# Revit family: 712-0620-001-DN40-300
name_source: partatom
category: Pipe Accessories
units: mm (PartAtom-declared; Revit-internal decimal feet)

## family parameters
Always vertical = Yes
Cut with Voids When Loaded = No
Part Type = Breaks Into
Round Connector Dimension = Use Diameter
Shared = No
Work Plane-Based = No

## types (13) — shared parameters
DN040_PN10/16 = 712-0040-06-201
DN050_PN10/16 = 712-0050-06-201
DN065_PN10/16 = 712-0065-06-201
DN080_PN10/16 = 712-0080-06-201
DN100 = No
DN100_PN10/16 = 712-0100-06-201
DN125 = No
DN125_PN10/16 = 712-0125-06-201
DN150 = No
DN150_PN10/16 = 712-0150-06-201
DN200_PN10 = 712-0200-06-200
DN200_PN16 = 712-0200-06-201
DN250 = No
DN250_PN10 = 712-0250-06-200
DN250_PN16 = 712-0250-06-201
DN300 = No
DN300_PN16 = 712-0300-06-201
DN40 = No
DN50 = No
DN65 = No
DN80 = No
Description_ = AVK FLANGED BEND 90° W/LOOSE FLANGES
Search_Table = 712-0620-001-DN40-300
URL product pages = https://www.avkvalves.com

## per-type parameters (varying)
| type | Body_wallthickness | CH | DN300_PN10 | F2 | FOD | Flange_thickness | H_width | Hole | ID | L | L_Ref | Nominal Diameter(DN) | RF_Thick | Rf_Dia | Rib_width |
| DN080_PN10/16 | 95 mm | 53 mm | 712-0300-06-200
712-0300-43-200 | 34 mm  [stored 0.111549 ft] | 100 mm | 17 mm  [stored 0.0557743 ft] | 7 mm  [stored 0.0229659 ft] | 5 mm  [stored 0.0164042 ft] | 40 mm  [stored 0.131234 ft] | 95 mm | 70 mm  [stored 0.229659 ft] | 80 mm  [stored 0.262467 ft] | 3 mm  [stored 0.00984252 ft] | 66 mm  [stored 0.216535 ft] | 20 mm  [stored 0.0656168 ft] |
| DN100_PN10/16 | 115 mm | 63 mm  [stored 0.206693 ft] | 712-0300-06-200 | 34 mm  [stored 0.111549 ft] | 110 mm | 17 mm  [stored 0.0557743 ft] | 7 mm  [stored 0.0229659 ft] | 5 mm  [stored 0.0164042 ft] | 50 mm  [stored 0.164042 ft] | 100 mm | 80 mm  [stored 0.262467 ft] | 100 mm | 3 mm  [stored 0.00984252 ft] | 78 mm  [stored 0.255906 ft] | 20 mm  [stored 0.0656168 ft] |
| DN150_PN10/16 | 165 mm | 88 mm | 712-0300-06-200 | 40 mm  [stored 0.131234 ft] | 143 mm | 20 mm  [stored 0.0656168 ft] | 8 mm  [stored 0.0262467 ft] | 5 mm  [stored 0.0164042 ft] | 75 mm | 120 mm | 100 mm | 150 mm | 4 mm  [stored 0.0131234 ft] | 106 mm | 25 mm  [stored 0.082021 ft] |
| DN040_PN10/16 | 55 mm  [stored 0.180446 ft] | 33 mm  [stored 0.108268 ft] | 712-0300-06-200 | 34 mm  [stored 0.111549 ft] | 75 mm | 17 mm  [stored 0.0557743 ft] | 5 mm  [stored 0.0164042 ft] | 3 mm  [stored 0.00984252 ft] | 20 mm  [stored 0.0656168 ft] | 100 mm | 40 mm  [stored 0.131234 ft] | 40 mm  [stored 0.131234 ft] | 3 mm  [stored 0.00984252 ft] | 42 mm  [stored 0.137795 ft] | 15 mm  [stored 0.0492126 ft] |
| DN050_PN10/16 | 65 mm  [stored 0.213255 ft] | 38 mm | 712-0300-06-200 | 34 mm  [stored 0.111549 ft] | 83 mm | 17 mm  [stored 0.0557743 ft] | 5 mm  [stored 0.0164042 ft] | 3 mm  [stored 0.00984252 ft] | 25 mm  [stored 0.082021 ft] | 100 mm | 50 mm  [stored 0.164042 ft] | 50 mm  [stored 0.164042 ft] | 3 mm  [stored 0.00984252 ft] | 50 mm  [stored 0.164042 ft] | 15 mm  [stored 0.0492126 ft] |
| DN065_PN10/16 | 80 mm  [stored 0.262467 ft] | 45 mm  [stored 0.147638 ft] | 712-0300-06-200 | 34 mm  [stored 0.111549 ft] | 93 mm | 17 mm  [stored 0.0557743 ft] | 5 mm  [stored 0.0164042 ft] | 3 mm  [stored 0.00984252 ft] | 33 mm  [stored 0.108268 ft] | 100 mm | 60 mm  [stored 0.19685 ft] | 65 mm  [stored 0.213255 ft] | 3 mm  [stored 0.00984252 ft] | 59 mm | 15 mm  [stored 0.0492126 ft] |
| DN200_PN10 | 215 mm | 113 mm | 712-0300-06-200 | 46 mm  [stored 0.150919 ft] | 170 mm | 23 mm  [stored 0.0754593 ft] | 8 mm  [stored 0.0262467 ft] | 5 mm  [stored 0.0164042 ft] | 100 mm | 150 mm | 110 mm | 200 mm | 4 mm  [stored 0.0131234 ft] | 133 mm | 25 mm  [stored 0.082021 ft] |
| DN250_PN10 | 265 mm | 138 mm | 712-0300-06-200 | 52 mm | 200 mm | 26 mm | 8 mm  [stored 0.0262467 ft] | 5 mm  [stored 0.0164042 ft] | 125 mm | 230 mm | 120 mm | 250 mm | 4 mm  [stored 0.0131234 ft] | 160 mm | 25 mm  [stored 0.082021 ft] |
| DN250_PN16 | 265 mm | 138 mm | 712-0300-06-200 | 52 mm | 200 mm | 26 mm | 8 mm  [stored 0.0262467 ft] | 5 mm  [stored 0.0164042 ft] | 125 mm | 230 mm | 120 mm | 250 mm | 4 mm  [stored 0.0131234 ft] | 160 mm | 25 mm  [stored 0.082021 ft] |
| DN200_PN16 | 215 mm | 113 mm | 712-0300-06-200 | 46 mm  [stored 0.150919 ft] | 170 mm | 23 mm  [stored 0.0754593 ft] | 8 mm  [stored 0.0262467 ft] | 5 mm  [stored 0.0164042 ft] | 100 mm | 150 mm | 110 mm | 200 mm | 4 mm  [stored 0.0131234 ft] | 133 mm | 25 mm  [stored 0.082021 ft] |
| DN300_PN10 | 315 mm | 163 mm | 712-0300-06-200 | 58 mm  [stored 0.190289 ft] | 228 mm | 29 mm  [stored 0.0951444 ft] | 10 mm  [stored 0.0328084 ft] | 5 mm  [stored 0.0164042 ft] | 150 mm | 270 mm | 130 mm | 300 mm | 4 mm  [stored 0.0131234 ft] | 185 mm | 30 mm  [stored 0.0984252 ft] |
| DN300_PN16 | 315 mm | 163 mm | 712-0300-06-200 | 58 mm  [stored 0.190289 ft] | 228 mm | 29 mm  [stored 0.0951444 ft] | 10 mm  [stored 0.0328084 ft] | 5 mm  [stored 0.0164042 ft] | 150 mm | 270 mm | 130 mm | 300 mm | 4 mm  [stored 0.0131234 ft] | 185 mm | 30 mm  [stored 0.0984252 ft] |
| DN125_PN10/16 | 140 mm | 75 mm | 712-0300-06-200 | 37 mm  [stored 0.121391 ft] | 125 mm | 19 mm | 7 mm  [stored 0.0229659 ft] | 5 mm  [stored 0.0164042 ft] | 63 mm  [stored 0.206693 ft] | 110 mm | 90 mm  [stored 0.295276 ft] | 125 mm | 3 mm  [stored 0.00984252 ft] | 92 mm | 20 mm  [stored 0.0656168 ft] |

note: [stored X ft] marks values corroborated as IEEE doubles in the binary element streams (Revit-internal decimal feet)

## geometry (parser evidence)
native form markers: Sweep x46
no freeform markers — native parametric forms only
